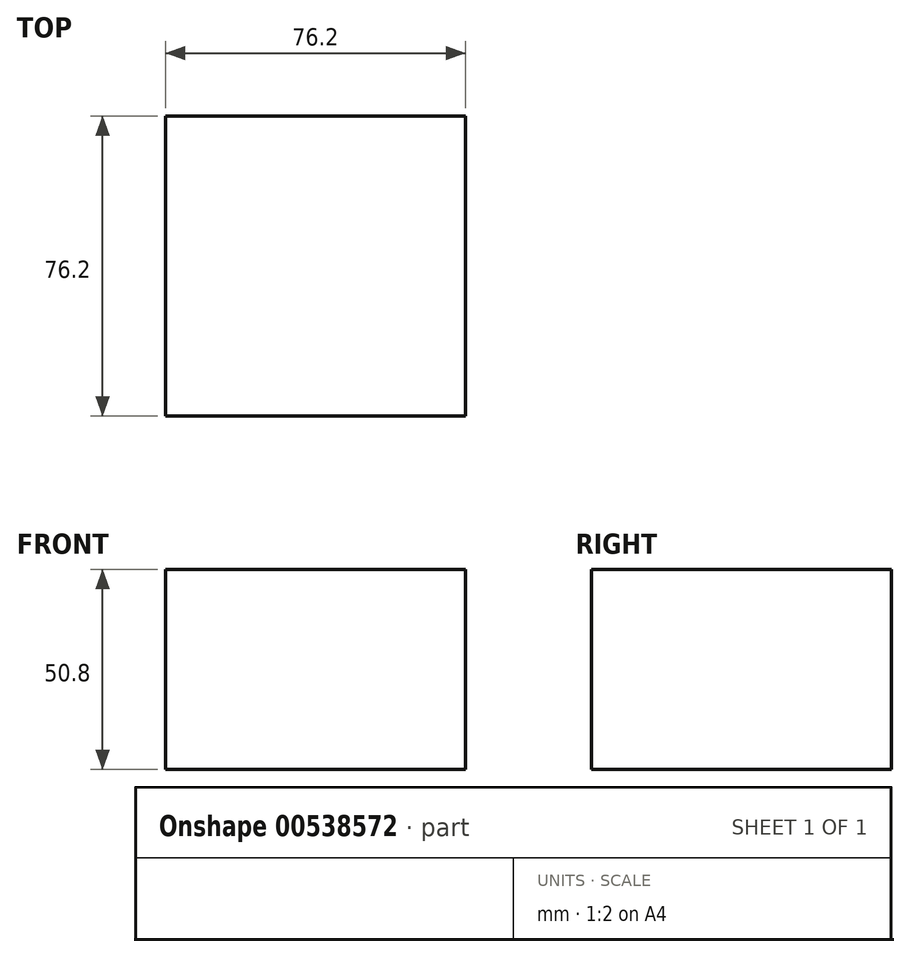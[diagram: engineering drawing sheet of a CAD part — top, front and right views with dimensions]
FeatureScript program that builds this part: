
annotation { "Feature Type Name" : "Feature", "Feature Type Description" : "" }
export const myFeature = defineFeature(function(context is Context, id is Id, definition is map)
    precondition{}
    {
        {
            var Q0;
            Q0=qCreatedBy(makeId("Top.planeOp"),FACE);
            var sketch = newSketch(context, id + "F0", { "sketchPlane" : qUnion([Q0])});
            skLineSegment(sketch, "E0.bottom", {"start": v(38.1, -38.1) * mm, "end": v(-38.1, -38.1) * mm});
            skLineSegment(sketch, "E0.top", {"start": v(38.1, 38.1) * mm, "end": v(-38.1, 38.1) * mm});
            skLineSegment(sketch, "E0.left", {"start": v(38.1, -38.1) * mm, "end": v(38.1, 38.1) * mm});
            skLineSegment(sketch, "E0.right", {"start": v(-38.1, -38.1) * mm, "end": v(-38.1, 38.1) * mm});
            skPoint(sketch, "E0.middle", {"position": v(0, 0) * mm});
            skSolve(sketch);
        }
        {
            var Q0;
            Q0 = qSketchRegion(id + "F0", true);
            extrude(context, id + "F1", {"entities" : qUnion([Q0]), "depth" : 50.8 * mm, "offsetDistance" : 25.4 * mm});
        }
    });
